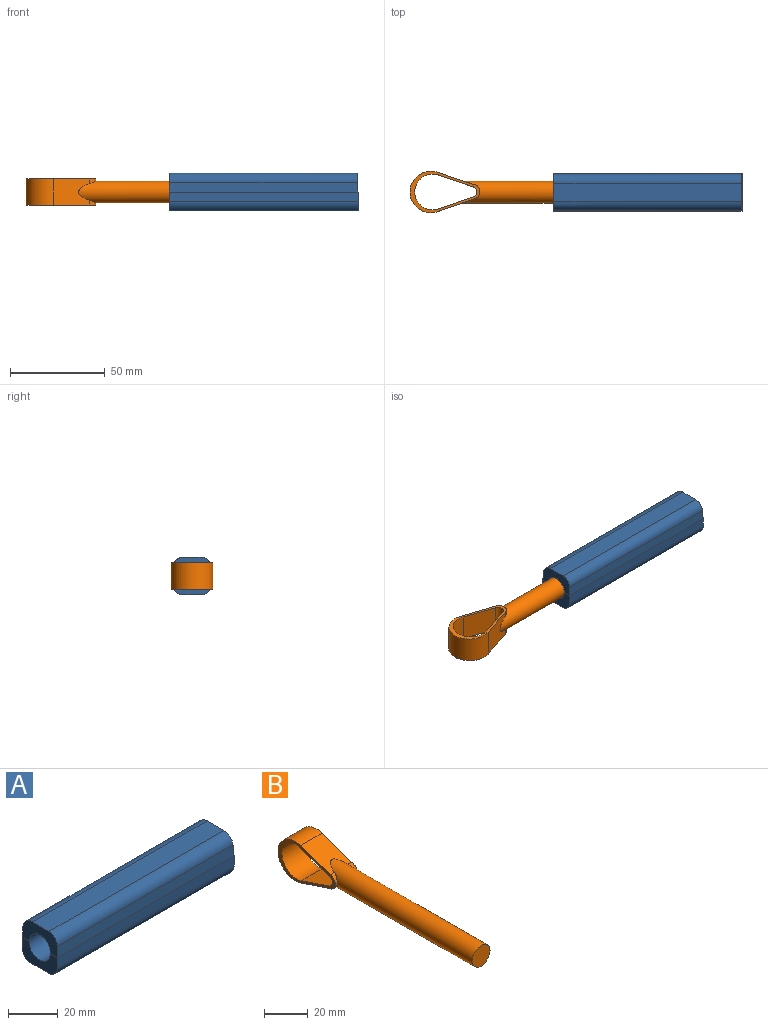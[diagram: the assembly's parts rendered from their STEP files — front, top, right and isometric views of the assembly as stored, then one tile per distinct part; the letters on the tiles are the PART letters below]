
ASSEMBLY  parts=2 mates=1
PART A: 16 faces, bbox 100x20x20 mm
  f0: plane 100x5.26mm, normal (0,-1,0.05), area 525.4mm2, adj f1,f3,f9,f13
  f1: plane 20x10mm, normal (1,0,0.05), area 185.5mm2, adj f0,f2,f4,f8,f12,f13
  f2: plane 100x5.26mm, normal (0,1,0.05), area 525.4mm2, adj f1,f3,f7,f12
  f3: plane 20x10mm, normal (-1,0,0.05), area 128.9mm2, adj f0,f2,f4,f6,f12,f13,f14
  f4: plane 98.95x9.46mm, normal (0,0,1), area 936.3mm2, adj f1,f3,f12,f13
  f5: plane 100x10mm, normal (0,0,-1), area 1000mm2, adj f6,f8,f10,f11
  f6: plane 20x10mm, normal (-1,0,0), area 132.7mm2, adj f3,f5,f7,f9,f10,f11,f14
  f7: plane 100x5mm, normal (0,1,0), area 500mm2, adj f2,f6,f8,f10
  f8: plane 20x10mm, normal (1,0,0), area 189.3mm2, adj f1,f5,f7,f9,f10,f11
  f9: plane 100x5mm, normal (0,-1,0), area 500mm2, adj f0,f6,f8,f11
  f10: cylinder r=5mm len=100mm, axis (-1,0,0), area 785.4mm2, adj f5,f6,f7,f8
  f11: cylinder r=5mm len=100mm, axis (1,0,0), area 785.4mm2, adj f5,f6,f8,f9
  f12: cylinder r=5mm len=99.45mm, axis (1,0,0), area 752.6mm2, adj f1,f2,f3,f4
  f13: cylinder r=5mm len=99.45mm, axis (-1,0,0), area 752.6mm2, adj f0,f1,f3,f4
  f14: cylinder r=6mm len=25mm, axis (-1,0,0), area 938.7mm2, adj f3,f6,f15
  f15: plane 12x12mm, normal (-1,0,0), area 113.1mm2, adj f14
PART B: 13 faces, bbox 14x124.1x22 mm
  f0: plane 37x22mm, normal (1,0,0), area 139.7mm2, adj f4,f6,f7,f8,f9,f10,f11,f12
  f1: plane 37x22mm, normal (-1,0,0), area 139.7mm2, adj f5,f6,f7,f8,f9,f10,f11,f12
  f2: cylinder r=5.75mm len=96.29mm, axis (0,1,0), area 3292.8mm2, adj f3,f4,f5,f6,f7
  f3: plane 11.5x11.5mm, normal (0,-1,0), area 103.9mm2, adj f2
  f4: cylinder r=4mm len=7.92mm, axis (-1,0,0), area 22.6mm2, adj f0,f2,f6,f7
  f5: cylinder r=4mm len=7.92mm, axis (-1,0,0), area 22.6mm2, adj f1,f2,f6,f7
  f6: plane 19.22x14mm, normal (0,-0.33,0.95), area 246.6mm2, adj f0,f1,f2,f4,f5,f8
  f7: plane 18.82x14mm, normal (0,-0.32,-0.95), area 251.6mm2, adj f0,f1,f2,f4,f5,f8
  f8: cylinder r=11mm len=22mm, axis (-1,0,0), area 583.8mm2, adj f0,f1,f6,f7
  f9: plane 19.36x14mm, normal (0,0.32,-0.95), area 286.3mm2, adj f0,f1,f10,f12
  f10: cylinder r=2.91mm len=14mm, axis (-1,0,0), area 101.3mm2, adj f0,f1,f9,f11
  f11: plane 18.21x14mm, normal (0,0.32,0.95), area 269.4mm2, adj f0,f1,f10,f12
  f12: cylinder r=9.51mm len=19.02mm, axis (-1,0,0), area 489.1mm2, adj f0,f1,f9,f11
PLACE A t=(8,-20.43,20.73)mm
PLACE B rot(axis=(0.58,-0.58,0.58),120deg) t=(-143.57,-10.43,20.73)mm
MATE parallel B.f2 <-> A.f14  axis (-1,0,0) through (-92,-10.43,20.73)mm
